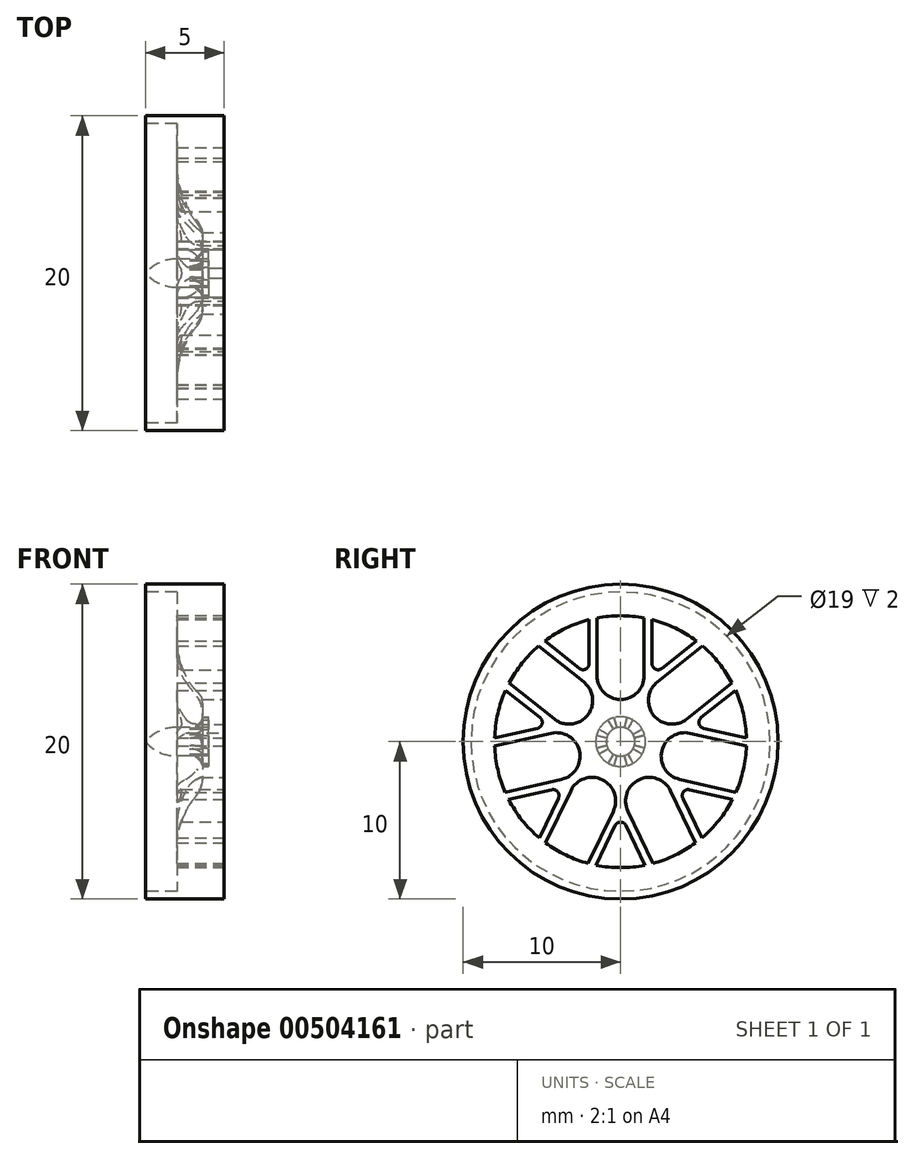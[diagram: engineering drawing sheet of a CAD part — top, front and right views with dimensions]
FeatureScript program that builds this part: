
annotation { "Feature Type Name" : "Feature", "Feature Type Description" : "" }
export const myFeature = defineFeature(function(context is Context, id is Id, definition is map)
    precondition{}
    {
        {
            var Q0;
            Q0=qCreatedBy(makeId("Front.planeOp"),FACE);
            var sketch = newSketch(context, id + "F0", { "sketchPlane" : qUnion([Q0])});
            skLineSegment(sketch, "E0", {"start": v(0, 10) * mm, "end": v(-3, 10) * mm});
            skLineSegment(sketch, "E1", {"start": v(-3, 10) * mm, "end": v(-3, 9.5) * mm});
            skLineSegment(sketch, "E2", {"start": v(-3, 9.5) * mm, "end": v(-1, 9.5) * mm});
            skArc(sketch, "E3", {"start": v(-1, 6.83) * mm, "mid": v(-0.67, 5) * mm, "end": v(0.26, 3.4) * mm});
            skLineSegment(sketch, "E4", {"start": v(0.62, 2.43) * mm, "end": v(0.62, 1.58) * mm});
            skLineSegment(sketch, "E5", {"start": v(-1, 0.92) * mm, "end": v(-0.2, 0.92) * mm});
            skLineSegment(sketch, "E6", {"start": v(-1, 6.83) * mm, "end": v(-1, 9.5) * mm});
            skPoint(sketch, "E7.visualSharp", {"position": v(0.62, 3.02) * mm});
            skArc(sketch, "E7.filletArc", {"start": v(0.62, 2.43) * mm, "mid": v(0.53, 2.94) * mm, "end": v(0.26, 3.4) * mm});
            skArc(sketch, "E8", {"start": v(-0.2, 0.92) * mm, "mid": v(0.33, 1.1) * mm, "end": v(0.62, 1.58) * mm});
            skArc(sketch, "E9", {"start": v(-1, 0.92) * mm, "mid": v(-2.1, 0.68) * mm, "end": v(-3, 0) * mm});
            skLineSegment(sketch, "E10", {"start": v(0, 10) * mm, "end": v(2, 10) * mm});
            skLineSegment(sketch, "E11", {"start": v(2, 10) * mm, "end": v(2, 0) * mm});
            skLineSegment(sketch, "E12", {"start": v(-4.03, 0) * mm, "end": v(5.95, 0) * mm, "construction": true});
            skLineSegment(sketch, "E13", {"start": v(-3, 0) * mm, "end": v(2, 0) * mm});
            skSolve(sketch);
        }
        {
            var Q0;
            Q0=makeQuery(id+"F0.imprint","IMPRINT",FACE,{"disambiguationData":[TD([[makeQuery(id+"F0.imprint","IMPRINT",EDGE,{"derivedFrom":sQuery(id+"F0.wireOp",EDGE,"E0")}),1.0]])]});
            var Q1;
            Q1=sQuery(id+"F0.wireOp",EDGE,"E12");
            revolve(context, id + "F1", {"entities" : qUnion([Q0]), "axis" : qUnion([Q1]), "revolveType" : RevolveType.FULL});
        }
        {
            var Q0;
            Q0=qCreatedBy(makeId("Right.planeOp"),FACE);
            var sketch = newSketch(context, id + "F2", { "sketchPlane" : qUnion([Q0])});
            skArc(sketch, "E14", {"start": v(1.5, 7.86) * mm, "mid": v(0, 8) * mm, "end": v(-1.5, 7.86) * mm});
            skLineSegment(sketch, "E15", {"start": v(-1.5, 7.86) * mm, "end": v(-1.5, 4.18) * mm});
            skArc(sketch, "E16", {"start": v(-1.5, 4.18) * mm, "mid": v(0, 2.68) * mm, "end": v(1.5, 4.18) * mm});
            skLineSegment(sketch, "E17", {"start": v(1.5, 4.18) * mm, "end": v(1.5, 7.86) * mm});
            skLineSegment(sketch, "E18.1.0", {"start": v(-7.08, 3.73) * mm, "end": v(-4.2, 1.44) * mm});
            skArc(sketch, "E18.1.1", {"start": v(-4.2, 1.44) * mm, "mid": v(-2.1, 1.67) * mm, "end": v(-2.34, 3.78) * mm});
            skLineSegment(sketch, "E18.1.2", {"start": v(-2.34, 3.78) * mm, "end": v(-5.2, 6.07) * mm});
            skLineSegment(sketch, "E18.2.0", {"start": v(-7.33, -3.21) * mm, "end": v(-3.75, -2.4) * mm});
            skArc(sketch, "E18.2.1", {"start": v(-3.75, -2.4) * mm, "mid": v(-2.62, -0.6) * mm, "end": v(-4.41, 0.53) * mm});
            skLineSegment(sketch, "E18.2.2", {"start": v(-4.41, 0.53) * mm, "end": v(-8, -0.29) * mm});
            skLineSegment(sketch, "E18.3.0", {"start": v(-2.06, -7.73) * mm, "end": v(-0.46, -4.42) * mm});
            skArc(sketch, "E18.3.1", {"start": v(-0.46, -4.42) * mm, "mid": v(-1.16, -2.42) * mm, "end": v(-3.17, -3.12) * mm});
            skLineSegment(sketch, "E18.3.2", {"start": v(-3.17, -3.12) * mm, "end": v(-4.76, -6.43) * mm});
            skLineSegment(sketch, "E18.4.0", {"start": v(4.76, -6.43) * mm, "end": v(3.17, -3.12) * mm});
            skArc(sketch, "E18.4.1", {"start": v(3.17, -3.12) * mm, "mid": v(1.16, -2.42) * mm, "end": v(0.46, -4.42) * mm});
            skLineSegment(sketch, "E18.4.2", {"start": v(0.46, -4.42) * mm, "end": v(2.06, -7.73) * mm});
            skLineSegment(sketch, "E18.5.0", {"start": v(8, -0.29) * mm, "end": v(4.41, 0.53) * mm});
            skArc(sketch, "E18.5.1", {"start": v(4.41, 0.53) * mm, "mid": v(2.62, -0.6) * mm, "end": v(3.75, -2.4) * mm});
            skLineSegment(sketch, "E18.5.2", {"start": v(3.75, -2.4) * mm, "end": v(7.33, -3.21) * mm});
            skLineSegment(sketch, "E18.6.0", {"start": v(5.2, 6.07) * mm, "end": v(2.34, 3.78) * mm});
            skArc(sketch, "E18.6.1", {"start": v(2.34, 3.78) * mm, "mid": v(2.1, 1.67) * mm, "end": v(4.2, 1.44) * mm});
            skLineSegment(sketch, "E18.6.2", {"start": v(4.2, 1.44) * mm, "end": v(7.08, 3.73) * mm});
            skLineSegment(sketch, "E19", {"start": v(-2, 7.75) * mm, "end": v(-2, 4.95) * mm});
            skLineSegment(sketch, "E20", {"start": v(-4.8, 6.4) * mm, "end": v(-2.62, 4.65) * mm});
            skArc(sketch, "E21", {"start": v(-2.62, 4.65) * mm, "mid": v(-2.22, 4.6) * mm, "end": v(-2, 4.95) * mm});
            skLineSegment(sketch, "E22.1.0", {"start": v(-7.3, 3.27) * mm, "end": v(-5.12, 1.52) * mm});
            skLineSegment(sketch, "E22.1.1", {"start": v(-8, 0.23) * mm, "end": v(-5.27, 0.85) * mm});
            skArc(sketch, "E22.1.2", {"start": v(-5.27, 0.85) * mm, "mid": v(-4.98, 1.14) * mm, "end": v(-5.12, 1.52) * mm});
            skLineSegment(sketch, "E22.2.0", {"start": v(-7.1, -3.67) * mm, "end": v(-4.38, -3.05) * mm});
            skLineSegment(sketch, "E22.2.1", {"start": v(-5.16, -6.11) * mm, "end": v(-3.95, -3.6) * mm});
            skArc(sketch, "E22.2.2", {"start": v(-3.95, -3.6) * mm, "mid": v(-4, -3.19) * mm, "end": v(-4.38, -3.05) * mm});
            skLineSegment(sketch, "E22.3.0", {"start": v(-1.56, -7.85) * mm, "end": v(-0.35, -5.33) * mm});
            skLineSegment(sketch, "E22.3.1", {"start": v(1.56, -7.85) * mm, "end": v(0.35, -5.33) * mm});
            skArc(sketch, "E22.3.2", {"start": v(0.35, -5.33) * mm, "mid": v(0, -5.11) * mm, "end": v(-0.35, -5.33) * mm});
            skLineSegment(sketch, "E22.4.0", {"start": v(5.16, -6.11) * mm, "end": v(3.95, -3.6) * mm});
            skLineSegment(sketch, "E22.4.1", {"start": v(7.1, -3.67) * mm, "end": v(4.38, -3.05) * mm});
            skArc(sketch, "E22.4.2", {"start": v(4.38, -3.05) * mm, "mid": v(4, -3.19) * mm, "end": v(3.95, -3.6) * mm});
            skLineSegment(sketch, "E22.5.0", {"start": v(8, 0.23) * mm, "end": v(5.27, 0.85) * mm});
            skLineSegment(sketch, "E22.5.1", {"start": v(7.3, 3.27) * mm, "end": v(5.12, 1.52) * mm});
            skArc(sketch, "E22.5.2", {"start": v(5.12, 1.52) * mm, "mid": v(4.98, 1.14) * mm, "end": v(5.27, 0.85) * mm});
            skLineSegment(sketch, "E22.6.0", {"start": v(4.8, 6.4) * mm, "end": v(2.62, 4.65) * mm});
            skLineSegment(sketch, "E22.6.1", {"start": v(2, 7.75) * mm, "end": v(2, 4.95) * mm});
            skArc(sketch, "E22.6.2", {"start": v(2, 4.95) * mm, "mid": v(2.22, 4.6) * mm, "end": v(2.62, 4.65) * mm});
            skArc(sketch, "E23.trimOffspring", {"start": v(-5.2, 6.07) * mm, "mid": v(-6.25, 4.99) * mm, "end": v(-7.08, 3.73) * mm});
            skArc(sketch, "E24.trimOffspring", {"start": v(-8, -0.29) * mm, "mid": v(-7.8, -1.78) * mm, "end": v(-7.33, -3.21) * mm});
            skArc(sketch, "E25.trimOffspring", {"start": v(-7.3, 3.27) * mm, "mid": v(-7.8, 1.78) * mm, "end": v(-8, 0.23) * mm});
            skArc(sketch, "E26.trimOffspring", {"start": v(-7.1, -3.67) * mm, "mid": v(-6.25, -4.99) * mm, "end": v(-5.16, -6.11) * mm});
            skArc(sketch, "E27.trimOffspring", {"start": v(-4.76, -6.43) * mm, "mid": v(-3.47, -7.2) * mm, "end": v(-2.06, -7.73) * mm});
            skArc(sketch, "E28.trimOffspring", {"start": v(-1.56, -7.85) * mm, "mid": v(0, -8) * mm, "end": v(1.56, -7.85) * mm});
            skArc(sketch, "E29.trimOffspring", {"start": v(2.06, -7.73) * mm, "mid": v(3.47, -7.2) * mm, "end": v(4.76, -6.43) * mm});
            skArc(sketch, "E30.trimOffspring", {"start": v(5.16, -6.11) * mm, "mid": v(6.25, -4.99) * mm, "end": v(7.1, -3.67) * mm});
            skArc(sketch, "E31.trimOffspring", {"start": v(7.33, -3.21) * mm, "mid": v(7.8, -1.78) * mm, "end": v(8, -0.29) * mm});
            skArc(sketch, "E32.trimOffspring", {"start": v(8, 0.23) * mm, "mid": v(7.8, 1.78) * mm, "end": v(7.3, 3.27) * mm});
            skArc(sketch, "E33.trimOffspring", {"start": v(7.08, 3.73) * mm, "mid": v(6.25, 4.99) * mm, "end": v(5.2, 6.07) * mm});
            skArc(sketch, "E34.trimOffspring", {"start": v(4.8, 6.4) * mm, "mid": v(3.47, 7.2) * mm, "end": v(2, 7.75) * mm});
            skArc(sketch, "E35", {"start": v(-2, 7.75) * mm, "mid": v(-3.47, 7.2) * mm, "end": v(-4.8, 6.4) * mm});
            skSolve(sketch);
        }
        {
            var Q0;
            Q0 = qSketchRegion(id + "F2", true);
            extrude(context, id + "F3", {"entities" : qUnion([Q0]), "operationType" : NewBodyOperationType.REMOVE, "oppositeDirection" : true, "depth" : 10 * mm, "hasSecondDirection" : true, "secondDirectionOppositeDirection" : false, "secondDirectionDepth" : 10 * mm});
        }
        {
            var Q0;
            Q0=qCreatedBy(makeId("Right.planeOp"),FACE);
            var sketch = newSketch(context, id + "F4", { "sketchPlane" : qUnion([Q0])});
            skArc(sketch, "E36.0", {"start": v(-0.41, 1.53) * mm, "mid": v(0, 1.58) * mm, "end": v(0.41, 1.53) * mm});
            skLineSegment(sketch, "E37", {"start": v(0.24, 0.88) * mm, "end": v(0.41, 1.53) * mm});
            skLineSegment(sketch, "E38", {"start": v(-0.24, 0.88) * mm, "end": v(-0.41, 1.53) * mm});
            skLineSegment(sketch, "E39.1.0", {"start": v(-0.46, 0.8) * mm, "end": v(-0.79, 1.37) * mm});
            skLineSegment(sketch, "E39.1.1", {"start": v(-0.8, 0.46) * mm, "end": v(-1.37, 0.79) * mm});
            skLineSegment(sketch, "E39.2.0", {"start": v(-0.88, 0.24) * mm, "end": v(-1.53, 0.41) * mm});
            skLineSegment(sketch, "E39.2.1", {"start": v(-0.88, -0.24) * mm, "end": v(-1.53, -0.41) * mm});
            skLineSegment(sketch, "E39.3.0", {"start": v(-0.8, -0.46) * mm, "end": v(-1.37, -0.79) * mm});
            skLineSegment(sketch, "E39.3.1", {"start": v(-0.46, -0.8) * mm, "end": v(-0.79, -1.37) * mm});
            skLineSegment(sketch, "E39.4.0", {"start": v(-0.24, -0.88) * mm, "end": v(-0.41, -1.53) * mm});
            skLineSegment(sketch, "E39.4.1", {"start": v(0.24, -0.88) * mm, "end": v(0.41, -1.53) * mm});
            skLineSegment(sketch, "E39.5.0", {"start": v(0.46, -0.8) * mm, "end": v(0.79, -1.37) * mm});
            skLineSegment(sketch, "E39.5.1", {"start": v(0.8, -0.46) * mm, "end": v(1.37, -0.79) * mm});
            skLineSegment(sketch, "E39.6.0", {"start": v(0.88, -0.24) * mm, "end": v(1.53, -0.41) * mm});
            skLineSegment(sketch, "E39.6.1", {"start": v(0.88, 0.24) * mm, "end": v(1.53, 0.41) * mm});
            skLineSegment(sketch, "E39.7.0", {"start": v(0.8, 0.46) * mm, "end": v(1.37, 0.79) * mm});
            skLineSegment(sketch, "E39.7.1", {"start": v(0.46, 0.8) * mm, "end": v(0.79, 1.37) * mm});
            skArc(sketch, "E40.trimOffspring", {"start": v(-1.37, 0.79) * mm, "mid": v(-1.12, 1.12) * mm, "end": v(-0.79, 1.37) * mm});
            skArc(sketch, "E41.trimOffspring", {"start": v(-1.53, -0.41) * mm, "mid": v(-1.58, 0) * mm, "end": v(-1.53, 0.41) * mm});
            skArc(sketch, "E42.trimOffspring", {"start": v(-0.79, -1.37) * mm, "mid": v(-1.12, -1.12) * mm, "end": v(-1.37, -0.79) * mm});
            skArc(sketch, "E43.trimOffspring", {"start": v(0.41, -1.53) * mm, "mid": v(0, -1.58) * mm, "end": v(-0.41, -1.53) * mm});
            skArc(sketch, "E44.trimOffspring", {"start": v(1.37, -0.79) * mm, "mid": v(1.12, -1.12) * mm, "end": v(0.79, -1.37) * mm});
            skArc(sketch, "E45.trimOffspring", {"start": v(1.53, 0.41) * mm, "mid": v(1.58, 0) * mm, "end": v(1.53, -0.41) * mm});
            skArc(sketch, "E46.trimOffspring", {"start": v(0.79, 1.37) * mm, "mid": v(1.12, 1.12) * mm, "end": v(1.37, 0.79) * mm});
            skArc(sketch, "E47.trimOffspring", {"start": v(-0.88, 0.24) * mm, "mid": v(-0.92, 0) * mm, "end": v(-0.88, -0.24) * mm});
            skArc(sketch, "E48.trimOffspring", {"start": v(-0.24, -0.88) * mm, "mid": v(0, -0.92) * mm, "end": v(0.24, -0.88) * mm});
            skArc(sketch, "E49.trimOffspring", {"start": v(0.88, -0.24) * mm, "mid": v(0.92, 0) * mm, "end": v(0.88, 0.24) * mm});
            skArc(sketch, "E50.trimOffspring", {"start": v(0.8, 0.46) * mm, "mid": v(0.65, 0.65) * mm, "end": v(0.46, 0.8) * mm});
            skArc(sketch, "E51.trimOffspring", {"start": v(0.24, 0.88) * mm, "mid": v(0, 0.92) * mm, "end": v(-0.24, 0.88) * mm});
            skArc(sketch, "E52.trimOffspring", {"start": v(0.46, -0.8) * mm, "mid": v(0.65, -0.65) * mm, "end": v(0.8, -0.46) * mm});
            skArc(sketch, "E53", {"start": v(-0.46, 0.8) * mm, "mid": v(-0.65, 0.65) * mm, "end": v(-0.8, 0.46) * mm});
            skArc(sketch, "E54", {"start": v(-0.8, -0.46) * mm, "mid": v(-0.65, -0.65) * mm, "end": v(-0.46, -0.8) * mm});
            skSolve(sketch);
        }
        {
            var Q0;
            Q0 = qSketchRegion(id + "F4", true);
            extrude(context, id + "F5", {"entities" : qUnion([Q0]), "operationType" : NewBodyOperationType.REMOVE, "oppositeDirection" : true, "depth" : .1946 * mm, "hasSecondDirection" : true, "secondDirectionOppositeDirection" : false, "secondDirectionDepth" : 1 * mm});
        }
    });
